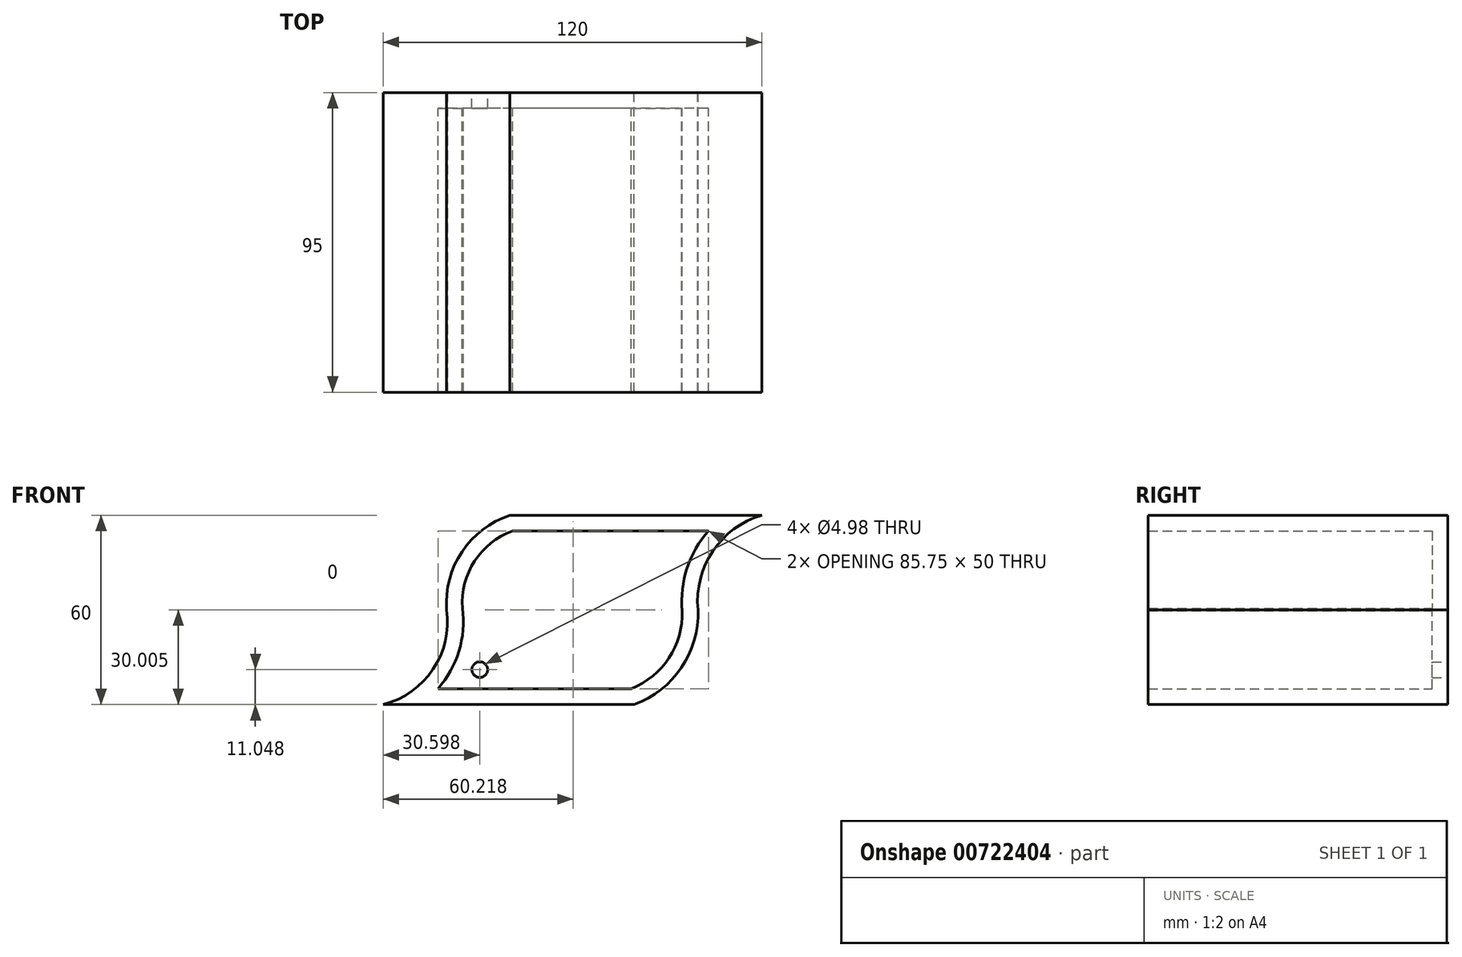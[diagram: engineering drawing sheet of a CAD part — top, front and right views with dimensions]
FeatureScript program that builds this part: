
annotation { "Feature Type Name" : "Feature", "Feature Type Description" : "" }
export const myFeature = defineFeature(function(context is Context, id is Id, definition is map)
    precondition{}
    {
        {
            var Q0;
            Q0=qCreatedBy(makeId("Front.planeOp"),FACE);
            var sketch = newSketch(context, id + "F0", { "sketchPlane" : qUnion([Q0])});
            skArc(sketch, "E0", {"start": v(-59.32, -32.6) * mm, "mid": v(-43.53, -21.44) * mm, "end": v(-39.2, -2.6) * mm});
            skArc(sketch, "E1", {"start": v(-19.16, 27.4) * mm, "mid": v(-34.36, 15.86) * mm, "end": v(-39.2, -2.6) * mm});
            skArc(sketch, "E2", {"start": v(60.68, 27.4) * mm, "mid": v(45.15, 16.05) * mm, "end": v(40.44, -2.6) * mm});
            skArc(sketch, "E3", {"start": v(20.22, -32.6) * mm, "mid": v(35.22, -20.9) * mm, "end": v(40.44, -2.6) * mm});
            skLineSegment(sketch, "E4", {"start": v(20.22, -32.6) * mm, "end": v(-59.32, -32.6) * mm});
            skLineSegment(sketch, "E5", {"start": v(60.68, 27.4) * mm, "end": v(-19.16, 27.4) * mm});
            skSolve(sketch);
        }
        {
            var Q0;
            Q0=makeQuery(id+"F0.imprint","IMPRINT",FACE,{"disambiguationData":[TD([[makeQuery(id+"F0.imprint","IMPRINT",EDGE,{"derivedFrom":sQuery(id+"F0.wireOp",EDGE,"E0")}),-1.0]])]});
            extrude(context, id + "F1", {"entities" : qUnion([Q0]), "depth" : 95 * mm, "offsetDistance" : 25 * mm});
        }
        {
            var Q0;
            Q0=makeQuery(id+"F1.opExtrude","CAP_FACE",FACE,{"disambiguationData":[OSD([sQuery(id+"F0.wireOp",EDGE,"E0"),sQuery(id+"F0.wireOp",EDGE,"E1"),sQuery(id+"F0.wireOp",EDGE,"E2"),sQuery(id+"F0.wireOp",EDGE,"E3"),sQuery(id+"F0.wireOp",EDGE,"E4"),sQuery(id+"F0.wireOp",EDGE,"E5")])],"isStart":false});
            shell(context, id + "F2", {"entities" : qUnion([Q0]), "thickness" : 5 * mm});
        }
        {
            var Q0;
            Q0=makeQuery(id+"F0.imprint","IMPRINT",FACE,{"disambiguationData":[TD([[makeQuery(id+"F0.imprint","IMPRINT",EDGE,{"derivedFrom":sQuery(id+"F0.wireOp",EDGE,"E0")}),-1.0]])]});
            var sketch = newSketch(context, id + "F3", { "sketchPlane" : qUnion([Q0])});
            skCircle(sketch, "E6", {"center": v(-28.72, -21.55) * mm, "radius": 2.5 * mm});
            skSolve(sketch);
        }
        {
            var Q0;
            Q0 = qSketchRegion(id + "F3", true);
            extrude(context, id + "F4", {"entities" : qUnion([Q0]), "operationType" : NewBodyOperationType.REMOVE, "depth" : 5 * mm, "offsetDistance" : 25 * mm});
        }
    });
